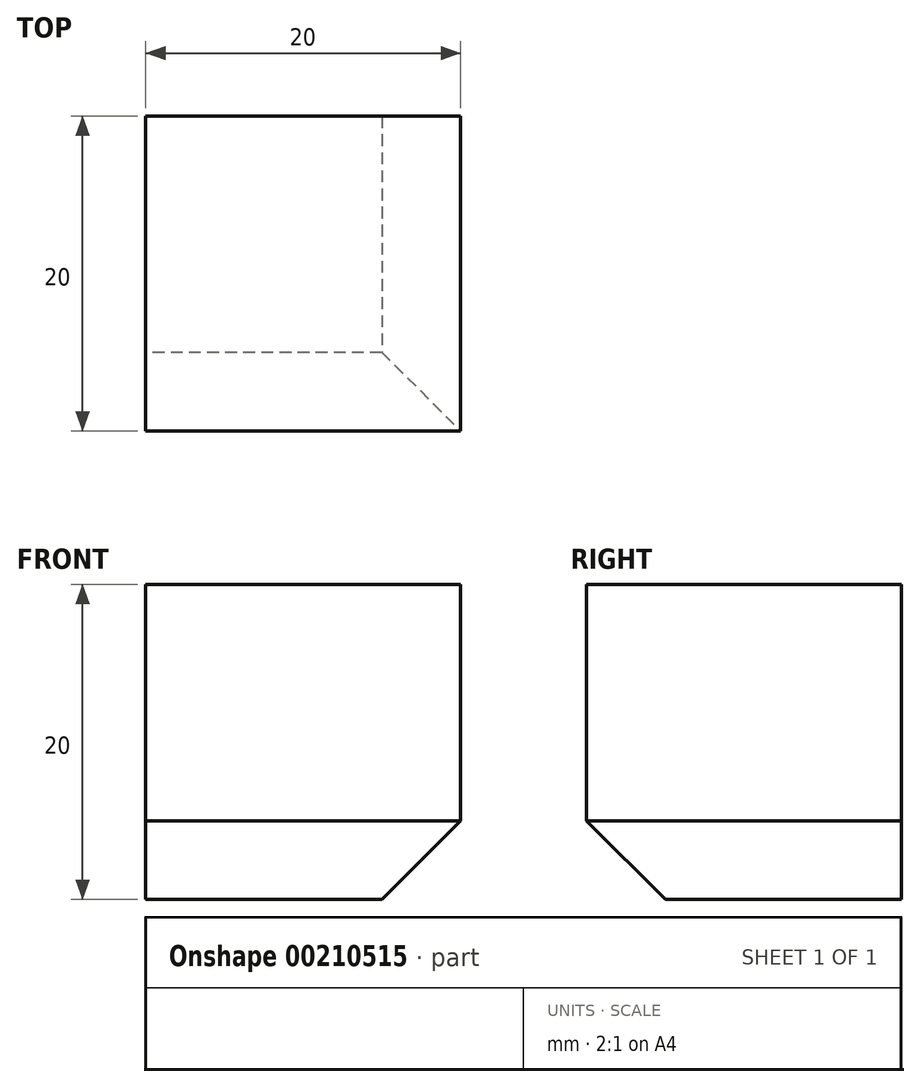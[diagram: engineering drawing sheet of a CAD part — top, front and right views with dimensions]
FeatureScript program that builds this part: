
annotation { "Feature Type Name" : "Feature", "Feature Type Description" : "" }
export const myFeature = defineFeature(function(context is Context, id is Id, definition is map)
    precondition{}
    {
        {
            var Q0;
            Q0=qCreatedBy(makeId("Top.planeOp"),FACE);
            var sketch = newSketch(context, id + "F0", { "sketchPlane" : qUnion([Q0])});
            skLineSegment(sketch, "E0.bottom", {"start": v(10, 10) * mm, "end": v(-10, 10) * mm});
            skLineSegment(sketch, "E0.top", {"start": v(10, -10) * mm, "end": v(-10, -10) * mm});
            skLineSegment(sketch, "E0.left", {"start": v(10, 10) * mm, "end": v(10, -10) * mm});
            skLineSegment(sketch, "E0.right", {"start": v(-10, 10) * mm, "end": v(-10, -10) * mm});
            skPoint(sketch, "E0.middle", {"position": v(0, 0) * mm});
            skSolve(sketch);
        }
        {
            var Q0;
            Q0 = qSketchRegion(id + "F0", true);
            extrude(context, id + "F1", {"entities" : qUnion([Q0]), "depth" : 20 * mm});
        }
        {
            var Q0;
            Q0=makeQuery(id+"F1.opExtrude","CAP_EDGE",EDGE,{"disambiguationData":[OSD([sQuery(id+"F0.wireOp",EDGE,"E0.top")])],"isStart":true});
            var Q1;
            Q1=makeQuery(id+"F1.opExtrude","CAP_EDGE",EDGE,{"disambiguationData":[OSD([sQuery(id+"F0.wireOp",EDGE,"E0.left")])],"isStart":true});
            chamfer(context, id + "F2", {"entities" : qUnion([Q0, Q1]), "width" : 5 * mm, "tangentPropagation" : true});
        }
    });
